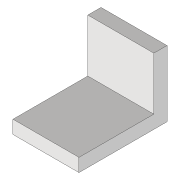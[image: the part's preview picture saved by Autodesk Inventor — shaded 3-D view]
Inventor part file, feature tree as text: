
AUTODESK INVENTOR PART (.ipt)
format: ipt  version: 2020 (Build 240168000, 168)  size: 93,696 bytes
history: native  units: mm
features: extrude x2, sketch x2
ambient origin geometry x8: Origin, YZ Plane, XZ Plane, XY Plane, X Axis, Y Axis, Z Axis, Center Point
bodies: Volumenkörper1 (feature_tree)
feature tree (4):
  extrude  "Extrusion1"  Depth=30.0mm
  extrude  "Extrusion2"  Depth=150.0mm
  sketch  "Skizze2"  dims[d0=30.0mm d1=30.0mm]
  sketch  "Skizze3"  dims[d2=200.0mm d3=150.0mm d4=150.0mm d5=0.0mm d6=150.0mm d7=20.0mm d8=40.0mm d9=65.0mm d10=30.0mm d11=0.0mm d12=0.0mm]
